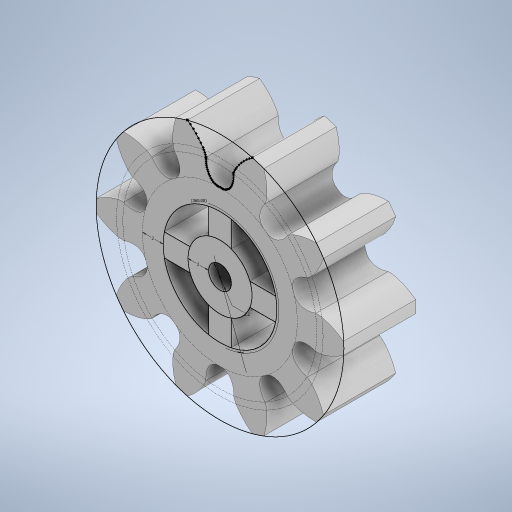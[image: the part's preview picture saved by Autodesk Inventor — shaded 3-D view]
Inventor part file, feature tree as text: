
AUTODESK INVENTOR PART (.ipt)
format: ipt  version: 2023 (Build 270158000, 158)  size: 404,480 bytes
history: native  units: mm
features: extrude x3, sketch x1, pattern_circular x1
ambient origin geometry x8: Origin, YZ Plane, XZ Plane, XY Plane, X Axis, Y Axis, Z Axis, Center Point
bodies: Solid1 (feature_tree)
feature tree (5):
  sketch  "Sketch1"  dims[d0=7.0mm d1=0.0mm d2=2.2mm d3=2.0mm d4=2.0mm d5=40.0mm d7=360.0deg d9=0.0mm d10=0.0mm d11=0.0mm d12=0.0mm d13=100.0mm d14=360.0deg]
  extrude  "Extrusion1"  Depth=2.2mm
  extrude  "Extrusion2"  Depth=2.0mm
  extrude  "Extrusion3"  Depth=2.0mm
  pattern_circular  "Circular Pattern1"  Count=4 Angle=360.0deg
